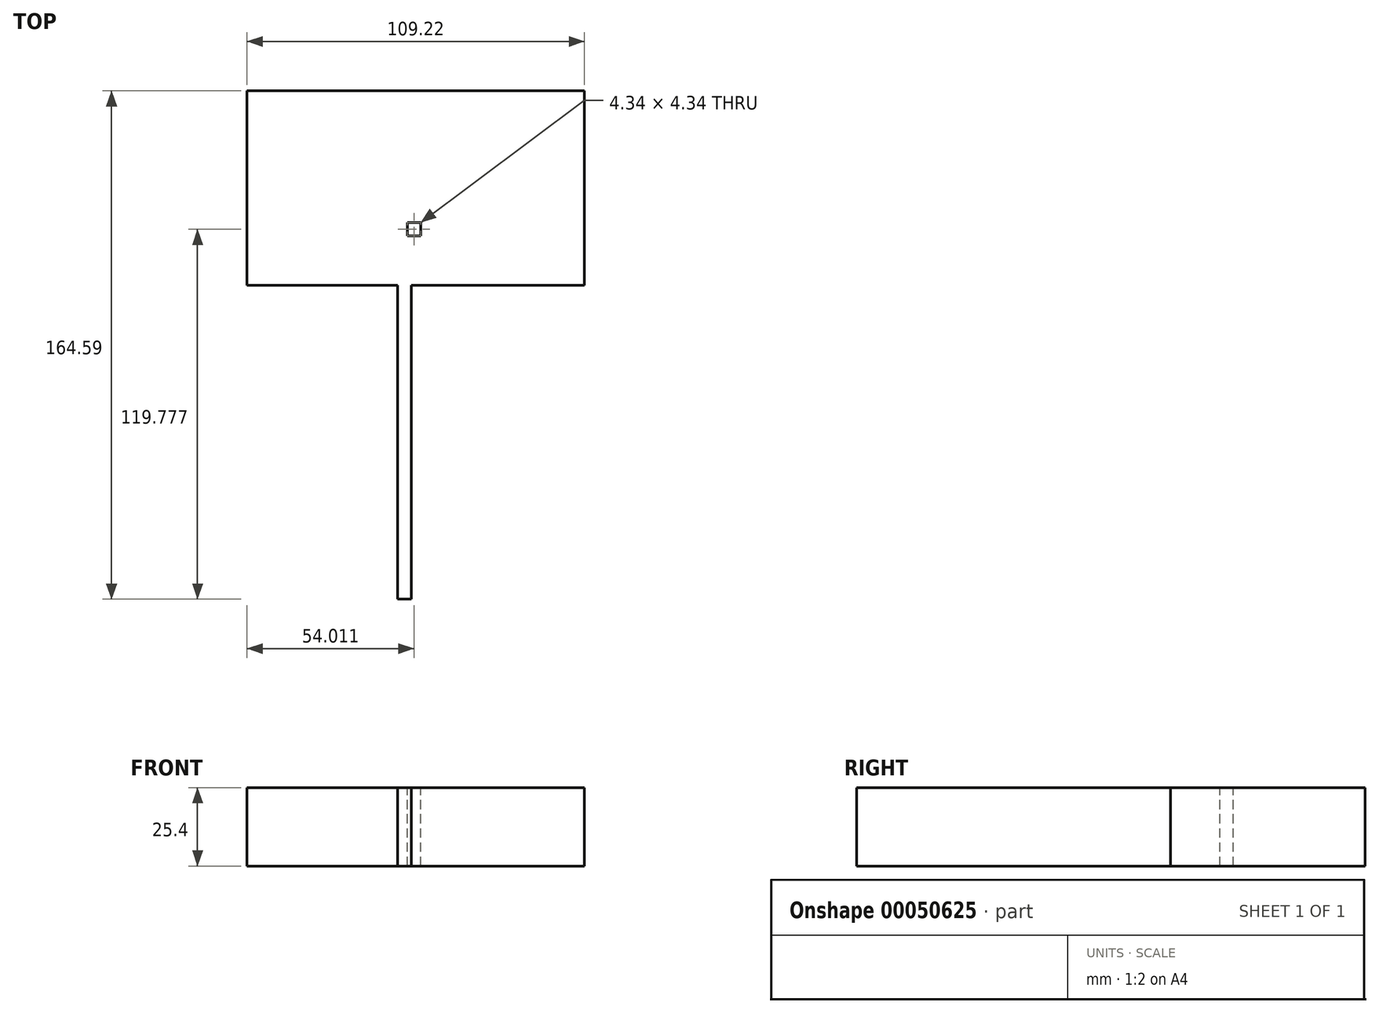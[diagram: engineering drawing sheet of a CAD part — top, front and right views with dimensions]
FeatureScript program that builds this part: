
annotation { "Feature Type Name" : "Feature", "Feature Type Description" : "" }
export const myFeature = defineFeature(function(context is Context, id is Id, definition is map)
    precondition{}
    {
        {
            var Q0;
            Q0=qCreatedBy(makeId("Top.planeOp"),FACE);
            var sketch = newSketch(context, id + "F0", { "sketchPlane" : qUnion([Q0])});
            skLineSegment(sketch, "E0.bottom", {"start": v(-41.68, 49.75) * mm, "end": v(67.54, 49.75) * mm});
            skLineSegment(sketch, "E0.top", {"start": v(-41.68, -13.24) * mm, "end": v(67.54, -13.24) * mm});
            skLineSegment(sketch, "E0.left", {"start": v(-41.68, 49.75) * mm, "end": v(-41.68, -13.24) * mm});
            skLineSegment(sketch, "E0.right", {"start": v(67.54, 49.75) * mm, "end": v(67.54, -13.24) * mm});
            skLineSegment(sketch, "E1.bottom", {"start": v(7.08, -13.24) * mm, "end": v(11.43, -13.24) * mm});
            skLineSegment(sketch, "E1.top", {"start": v(7.08, -114.84) * mm, "end": v(11.43, -114.84) * mm});
            skLineSegment(sketch, "E1.left", {"start": v(7.08, -13.24) * mm, "end": v(7.08, -114.84) * mm});
            skLineSegment(sketch, "E1.right", {"start": v(11.43, -13.24) * mm, "end": v(11.43, -114.84) * mm});
            skSolve(sketch);
        }
        {
            var Q0;
            Q0 = qSketchRegion(id + "F0", true);
            extrude(context, id + "F1", {"entities" : qUnion([Q0]), "depth" : 25.4 * mm});
        }
        {
            var Q0;
            Q0=makeQuery(id+"F1.opExtrude","CAP_FACE",FACE,{"disambiguationData":[OSD([sQuery(id+"F0.wireOp",EDGE,"E0.bottom"),sQuery(id+"F0.wireOp",EDGE,"E0.top"),sQuery(id+"F0.wireOp",EDGE,"E0.left"),sQuery(id+"F0.wireOp",EDGE,"E0.right"),sQuery(id+"F0.wireOp",EDGE,"E1.top"),sQuery(id+"F0.wireOp",EDGE,"E1.left"),sQuery(id+"F0.wireOp",EDGE,"E1.right")])],"isStart":false});
            var sketch = newSketch(context, id + "F2", { "sketchPlane" : qUnion([Q0])});
            skLineSegment(sketch, "E2.bottom", {"start": v(10.16, 2.77) * mm, "end": v(14.5, 2.77) * mm});
            skLineSegment(sketch, "E2.top", {"start": v(10.16, 7.1) * mm, "end": v(14.5, 7.1) * mm});
            skLineSegment(sketch, "E2.left", {"start": v(10.16, 2.77) * mm, "end": v(10.16, 7.1) * mm});
            skLineSegment(sketch, "E2.right", {"start": v(14.5, 2.77) * mm, "end": v(14.5, 7.1) * mm});
            skSolve(sketch);
        }
        {
            var Q0;
            Q0=makeQuery(id+"F2.imprint","IMPRINT",FACE,{"disambiguationData":[TD([[makeQuery(id+"F2.imprint","IMPRINT",EDGE,{"derivedFrom":sQuery(id+"F2.wireOp",EDGE,"E2.bottom")}),1.0]])]});
            extrude(context, id + "F3", {"entities" : qUnion([Q0]), "operationType" : NewBodyOperationType.REMOVE, "endBound" : BoundingType.THROUGH_ALL, "oppositeDirection" : true, "depth" : 25.4 * mm});
        }
    });
